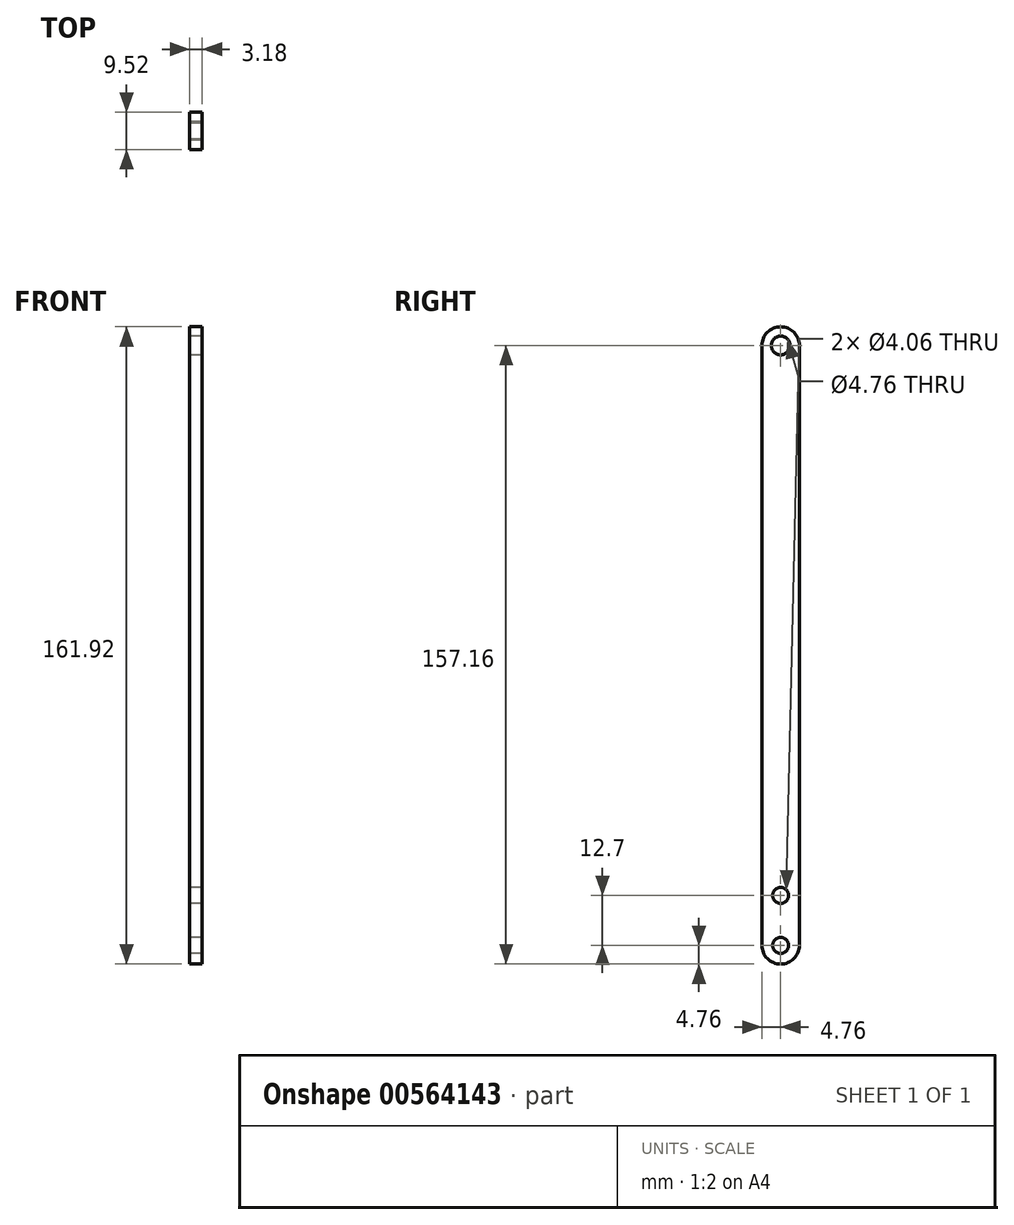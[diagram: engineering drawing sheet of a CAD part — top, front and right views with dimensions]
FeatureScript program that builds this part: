
annotation { "Feature Type Name" : "Feature", "Feature Type Description" : "" }
export const myFeature = defineFeature(function(context is Context, id is Id, definition is map)
    precondition{}
    {
        {
            var Q0;
            Q0=qCreatedBy(makeId("Right.planeOp"),FACE);
            var sketch = newSketch(context, id + "F0", { "sketchPlane" : qUnion([Q0])});
            skCircle(sketch, "E0", {"center": v(0, 0) * mm, "radius": 2.03 * mm});
            skCircle(sketch, "E1", {"center": v(0, 152.4) * mm, "radius": 2.38 * mm});
            skCircle(sketch, "E2", {"center": v(0, 152.4) * mm, "radius": 4.76 * mm});
            skArc(sketch, "E3", {"start": v(-4.76, 0) * mm, "mid": v(0, -4.76) * mm, "end": v(4.76, 0) * mm});
            skLineSegment(sketch, "E4", {"start": v(-4.76, 152.4) * mm, "end": v(-4.76, 0) * mm});
            skLineSegment(sketch, "E5", {"start": v(4.76, 152.4) * mm, "end": v(4.76, 0) * mm});
            skCircle(sketch, "E6", {"center": v(0, 12.7) * mm, "radius": 2.03 * mm});
            skSolve(sketch);
        }
        {
            var Q0;
            Q0=qSketchRegion(id+"F0",true);
            extrude(context, id + "F1", {"entities" : qUnion([Q0]), "depth" : 3.17 * mm, "offsetDistance" : 25.4 * mm});
        }
    });
